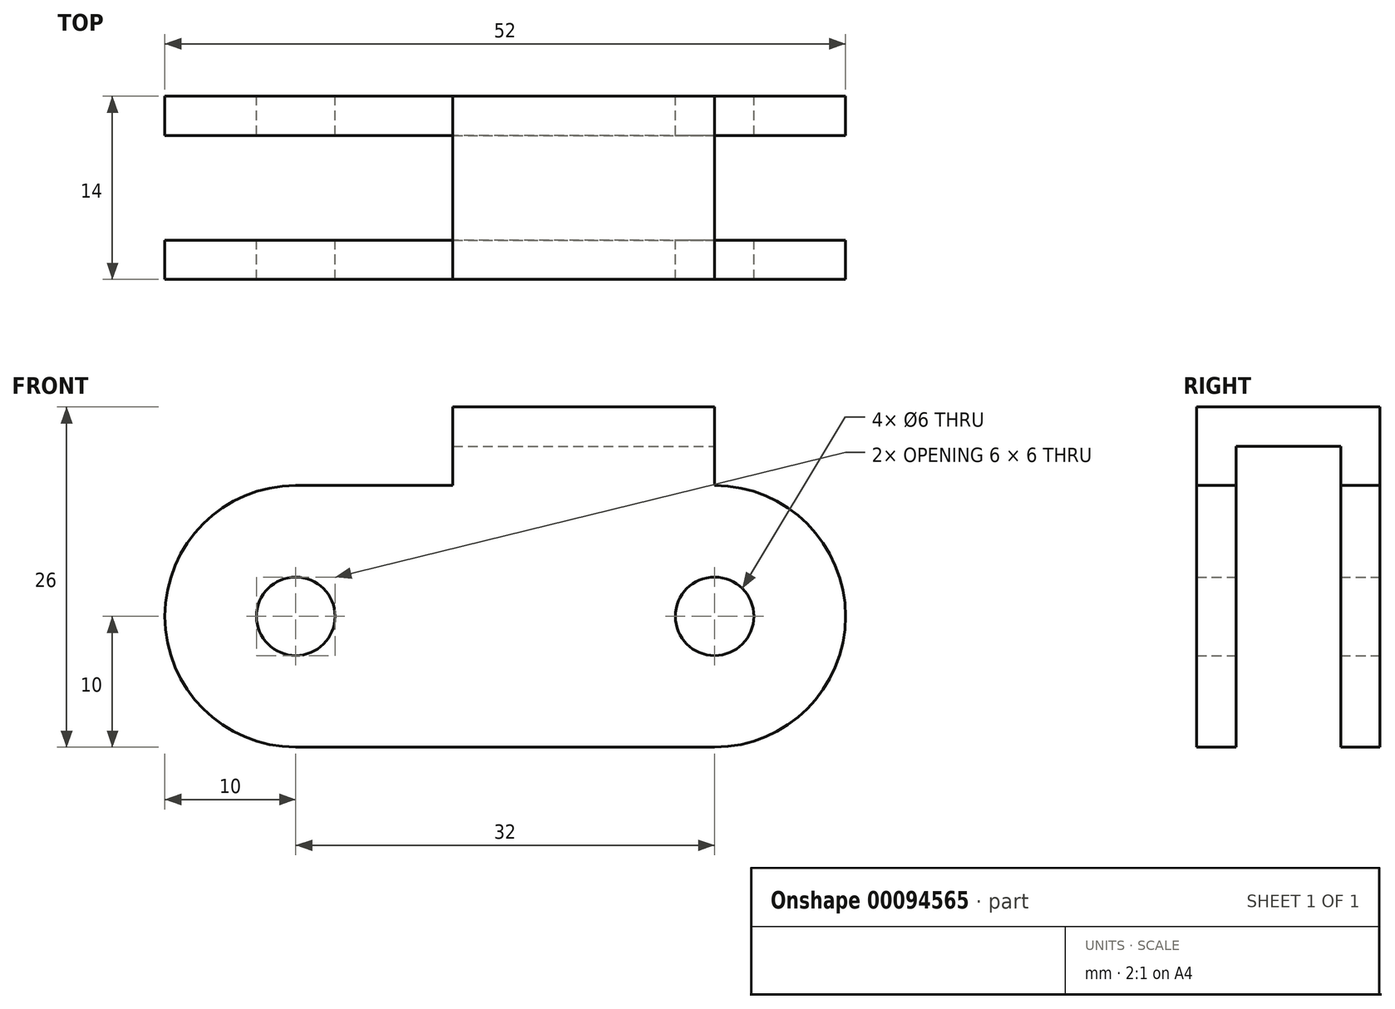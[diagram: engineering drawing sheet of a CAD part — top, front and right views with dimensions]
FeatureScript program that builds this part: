
annotation { "Feature Type Name" : "Feature", "Feature Type Description" : "" }
export const myFeature = defineFeature(function(context is Context, id is Id, definition is map)
    precondition{}
    {
        {
            var Q0;
            Q0=qCreatedBy(makeId("Front.planeOp"),FACE);
            var sketch = newSketch(context, id + "F0", { "sketchPlane" : qUnion([Q0])});
            skLineSegment(sketch, "E0", {"start": v(-32, 0) * mm, "end": v(0, 0) * mm});
            skArc(sketch, "E1.0.startCap", {"start": v(-32, -10) * mm, "mid": v(-42, 0) * mm, "end": v(-32, 10) * mm});
            skArc(sketch, "E1.0.endCap", {"start": v(0, 10) * mm, "mid": v(10, 0) * mm, "end": v(0, -10) * mm});
            skLineSegment(sketch, "E1.0.left", {"start": v(-32, 10) * mm, "end": v(0, 10) * mm});
            skLineSegment(sketch, "E1.0.right", {"start": v(-32, -10) * mm, "end": v(0, -10) * mm});
            skCircle(sketch, "E2", {"center": v(-32, 0) * mm, "radius": 3 * mm});
            skCircle(sketch, "E3.1.0.0", {"center": v(0, 0) * mm, "radius": 3 * mm});
            skLineSegment(sketch, "E3.direction1", {"start": v(-32, 0) * mm, "end": v(0, 0) * mm, "construction": true});
            skLineSegment(sketch, "E4.bottom", {"start": v(0, 10) * mm, "end": v(-20, 10) * mm});
            skLineSegment(sketch, "E4.top", {"start": v(0, 16) * mm, "end": v(-20, 16) * mm});
            skLineSegment(sketch, "E4.left", {"start": v(0, 10) * mm, "end": v(0, 16) * mm});
            skLineSegment(sketch, "E4.right", {"start": v(-20, 10) * mm, "end": v(-20, 16) * mm});
            skSolve(sketch);
        }
        {
            var Q0;
            Q0 = qSketchRegion(id + "F0", true);
            extrude(context, id + "F1", {"entities" : qUnion([Q0]), "endBound" : BoundingType.SYMMETRIC, "depth" : 14 * mm});
        }
        {
            var Q0;
            Q0=qCreatedBy(makeId("Right.planeOp"),FACE);
            var sketch = newSketch(context, id + "F2", { "sketchPlane" : qUnion([Q0])});
            skLineSegment(sketch, "E5.bottom", {"start": v(-4, -13) * mm, "end": v(4, -13) * mm});
            skLineSegment(sketch, "E5.top", {"start": v(-4, 13) * mm, "end": v(4, 13) * mm});
            skLineSegment(sketch, "E5.left", {"start": v(-4, -13) * mm, "end": v(-4, 13) * mm});
            skLineSegment(sketch, "E5.right", {"start": v(4, -13) * mm, "end": v(4, 13) * mm});
            skPoint(sketch, "E5.middle", {"position": v(0, 0) * mm});
            skSolve(sketch);
        }
        {
            var Q0;
            Q0 = qSketchRegion(id + "F2", true);
            extrude(context, id + "F3", {"entities" : qUnion([Q0]), "operationType" : NewBodyOperationType.REMOVE, "endBound" : BoundingType.SYMMETRIC, "oppositeDirection" : true, "depth" : 100.25 * mm});
        }
    });
